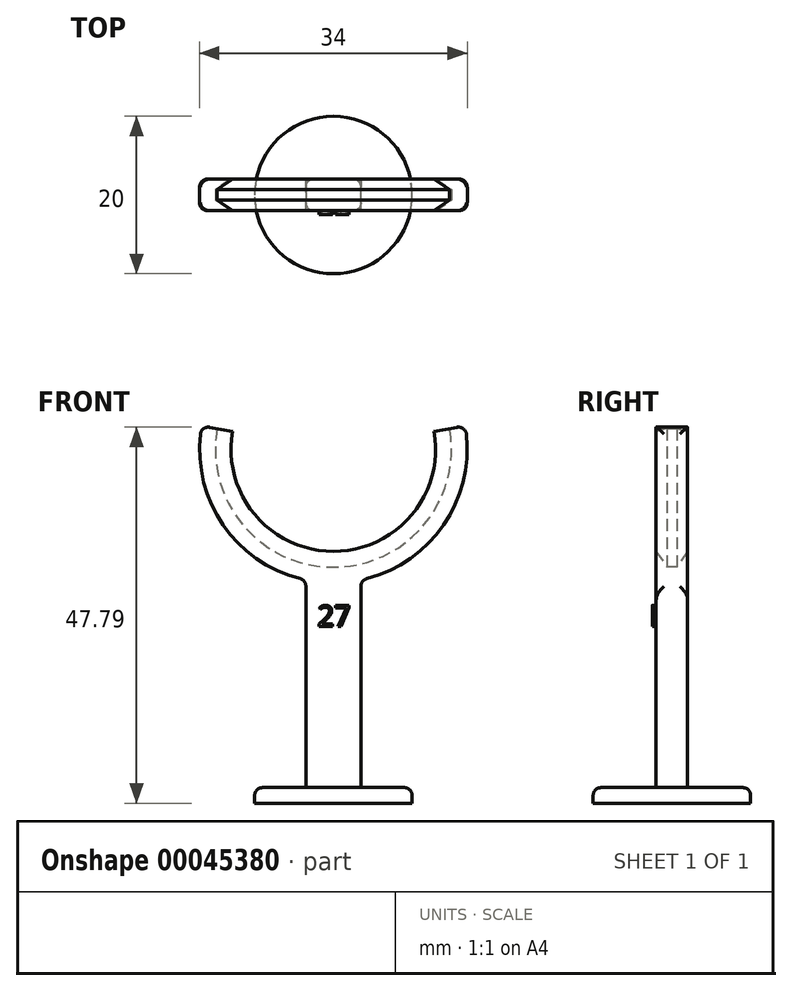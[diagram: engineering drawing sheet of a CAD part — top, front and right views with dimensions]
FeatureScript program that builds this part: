
annotation { "Feature Type Name" : "Feature", "Feature Type Description" : "" }
export const myFeature = defineFeature(function(context is Context, id is Id, definition is map)
    precondition{}
    {
        {
            var Q0;
            Q0=qCreatedBy(makeId("Top.planeOp"),FACE);
            var sketch = newSketch(context, id + "F0", { "sketchPlane" : qUnion([Q0])});
            skCircle(sketch, "E0", {"center": v(0, 0) * mm, "radius": 10 * mm});
            skSolve(sketch);
        }
        {
            var Q0;
            Q0=makeQuery(id+"F0.imprint","IMPRINT",FACE,{"disambiguationData":[TD([[makeQuery(id+"F0.imprint","IMPRINT",EDGE,{"derivedFrom":sQuery(id+"F0.wireOp",EDGE,"E0")}),1.0]])]});
            extrude(context, id + "F1", {"entities" : qUnion([Q0]), "depth" : 2 * mm});
        }
        {
            var Q0;
            Q0=qCreatedBy(makeId("Front.planeOp"),FACE);
            var sketch = newSketch(context, id + "F2", { "sketchPlane" : qUnion([Q0])});
            skLineSegment(sketch, "E1", {"start": v(0, 0) * mm, "end": v(0, 45) * mm, "construction": true});
            skLineSegment(sketch, "E2", {"start": v(-13, 45) * mm, "end": v(13, 45) * mm, "construction": true});
            skCircle(sketch, "E3", {"center": v(0, 45) * mm, "radius": 13 * mm, "construction": true});
            skLineSegment(sketch, "E4", {"start": v(-12.8, 47.26) * mm, "end": v(0, 45) * mm, "construction": true});
            skLineSegment(sketch, "E5", {"start": v(-12.8, 47.26) * mm, "end": v(-16.74, 47.95) * mm});
            skLineSegment(sketch, "E6.MirrorCS", {"start": v(12.8, 47.26) * mm, "end": v(16.74, 47.95) * mm});
            skArc(sketch, "E7", {"start": v(-16.74, 47.95) * mm, "mid": v(0, 28) * mm, "end": v(16.74, 47.95) * mm});
            skArc(sketch, "E8", {"start": v(-12.8, 47.26) * mm, "mid": v(0, 32) * mm, "end": v(12.8, 47.26) * mm});
            skLineSegment(sketch, "E9", {"start": v(-3.5, 28.36) * mm, "end": v(3.5, 28.36) * mm, "construction": true});
            skLineSegment(sketch, "E10.0", {"start": v(-10, 2) * mm, "end": v(10, 2) * mm, "construction": true});
            skLineSegment(sketch, "E11", {"start": v(-3.5, 28.36) * mm, "end": v(-3.5, 2) * mm});
            skLineSegment(sketch, "E12.MirrorCS", {"start": v(3.5, 28.36) * mm, "end": v(3.5, 2) * mm});
            skLineSegment(sketch, "E13", {"start": v(-3.5, 2) * mm, "end": v(3.5, 2) * mm});
            skSolve(sketch);
        }
        {
            var Q0;
            Q0 = qSketchRegion(id + "F2", true);
            extrude(context, id + "F3", {"entities" : qUnion([Q0]), "operationType" : NewBodyOperationType.ADD, "endBound" : BoundingType.SYMMETRIC, "depth" : 4 * mm, "hasSecondDirection" : true, "secondDirectionOppositeDirection" : true, "secondDirectionDepth" : 1.5 * mm});
        }
        {
            var Q0;
            Q0=makeQuery(id+"F3.opExtrude","CAP_EDGE",EDGE,{"disambiguationData":[OSD([sQuery(id+"F2.wireOp",EDGE,"E8")])],"isStart":false});
            var Q1;
            Q1=makeQuery(id+"F3.opExtrude","CAP_VERTEX",VERTEX,{"disambiguationData":[OSD([sQuery(id+"F2.wireOp",EDGE,"E5"),sQuery(id+"F2.wireOp",EDGE,"E8")])],"isStart":false});
            cPlane(context, id + "F4", {"entities" : qUnion([Q0, Q1]), "cplaneType" : CPlaneType.CURVE_POINT, "offset" : 150 * mm, "width" : 150 * mm, "height" : 150 * mm});
        }
        {
            var Q0;
            Q0=qCreatedBy(id+"F4.planeOp",FACE);
            var sketch = newSketch(context, id + "F5", { "sketchPlane" : qUnion([Q0])});
            skPoint(sketch, "E14.0", {"position": v(-20.81, 2) * mm});
            skLineSegment(sketch, "E15.0", {"start": v(-20.81, 2) * mm, "end": v(-20.81, -2) * mm});
            skLineSegment(sketch, "E16", {"start": v(-20.81, 0) * mm, "end": v(-22.81, 0) * mm, "construction": true});
            skLineSegment(sketch, "E17", {"start": v(-22.81, 0.65) * mm, "end": v(-22.81, -0.65) * mm});
            skLineSegment(sketch, "E18", {"start": v(-22.81, 0.65) * mm, "end": v(-20.81, 2) * mm});
            skLineSegment(sketch, "E19", {"start": v(-22.81, -0.65) * mm, "end": v(-20.81, -2) * mm});
            skSolve(sketch);
        }
        {
            var Q0;
            Q0=makeQuery(id+"F5.imprint","IMPRINT",FACE,{"disambiguationData":[TD([[makeQuery(id+"F5.imprint","IMPRINT",EDGE,{"derivedFrom":sQuery(id+"F5.wireOp",EDGE,"E15.0")}),-1.0]])]});
            var Q1;
            Q1=makeQuery(id+"F3.opExtrude","CAP_EDGE",EDGE,{"disambiguationData":[OSD([sQuery(id+"F2.wireOp",EDGE,"E8")])],"isStart":false});
            sweep(context, id + "F6", {"operationType" : NewBodyOperationType.REMOVE, "profiles" : qUnion([Q0]), "path" : qUnion([Q1])});
        }
        {
            var Q0;
            {var subQ0=sQuery(id+"F2.wireOp",EDGE,"E7");Q0=makeQuery(id+"F3.opExtrude","SWEPT_FACE",FACE,{"disambiguationData":[OSD([subQ0]),TDD([makeQuery(id+"F2.imprint","IMPRINT",EDGE,{"disambiguationData":[TD([[makeQuery(id+"F2.imprint","INTERSECT",VERTEX,{"derivedFrom":[sQuery(id+"F2.wireOp",EDGE,"E5"),subQ0]}),-1.0]])],"derivedFrom":subQ0})])]});}
            var Q1;
            {var subQ0=sQuery(id+"F2.wireOp",EDGE,"E7");Q1=makeQuery(id+"F3.opExtrude","SWEPT_FACE",FACE,{"disambiguationData":[OSD([subQ0]),TDD([makeQuery(id+"F2.imprint","IMPRINT",EDGE,{"disambiguationData":[TD([[makeQuery(id+"F2.imprint","INTERSECT",VERTEX,{"derivedFrom":[sQuery(id+"F2.wireOp",EDGE,"E6.MirrorCS"),subQ0]}),1.0]])],"derivedFrom":subQ0})])]});}
            var Q2;
            Q2=makeQuery(id+"F3.opExtrude","CAP_EDGE",EDGE,{"disambiguationData":[OSD([sQuery(id+"F2.wireOp",EDGE,"E13")])],"isStart":false});
            var Q3;
            Q3=makeQuery(id+"F1.opExtrude","CAP_EDGE",EDGE,{"disambiguationData":[OSD([sQuery(id+"F0.wireOp",EDGE,"E0")])],"isStart":false});
            fillet(context, id + "F7", {"entities" : qUnion([Q0, Q1, Q2, Q3]), "radius" : 1 * mm, "tangentPropagation" : true, "allowEdgeOverflow" : false});
        }
        {
            var Q0;
            Q0=makeQuery(id+"F3.opExtrude","CAP_FACE",FACE,{"disambiguationData":[OSD([sQuery(id+"F2.wireOp",EDGE,"E5"),sQuery(id+"F2.wireOp",EDGE,"E6.MirrorCS"),sQuery(id+"F2.wireOp",EDGE,"E7"),sQuery(id+"F2.wireOp",EDGE,"E8"),sQuery(id+"F2.wireOp",EDGE,"E11"),sQuery(id+"F2.wireOp",EDGE,"E12.MirrorCS"),sQuery(id+"F2.wireOp",EDGE,"E13")])],"isStart":false});
            var sketch = newSketch(context, id + "F8", { "sketchPlane" : qUnion([Q0])});
            skText(sketch, "E20", { "text": "27", "fontName": "OpenSans-Regular.ttf"});
            skPoint(sketch, "E21.1", {"position": v(0, 0) * mm});
            skLineSegment(sketch, "E22.0", {"start": v(0, 0) * mm, "end": v(0, 45) * mm, "construction": true});
            const initialGuessF8  = {"E20": [-0.002, 0.0225, 1, 0, 0.00264]};
            skSetInitialGuess(sketch, initialGuessF8);
            skSolve(sketch);
        }
        {
            var Q0;
            Q0 = qSketchRegion(id + "F8", true);
            extrude(context, id + "F9", {"entities" : qUnion([Q0]), "operationType" : NewBodyOperationType.ADD, "depth" : .5 * mm});
        }
    });
